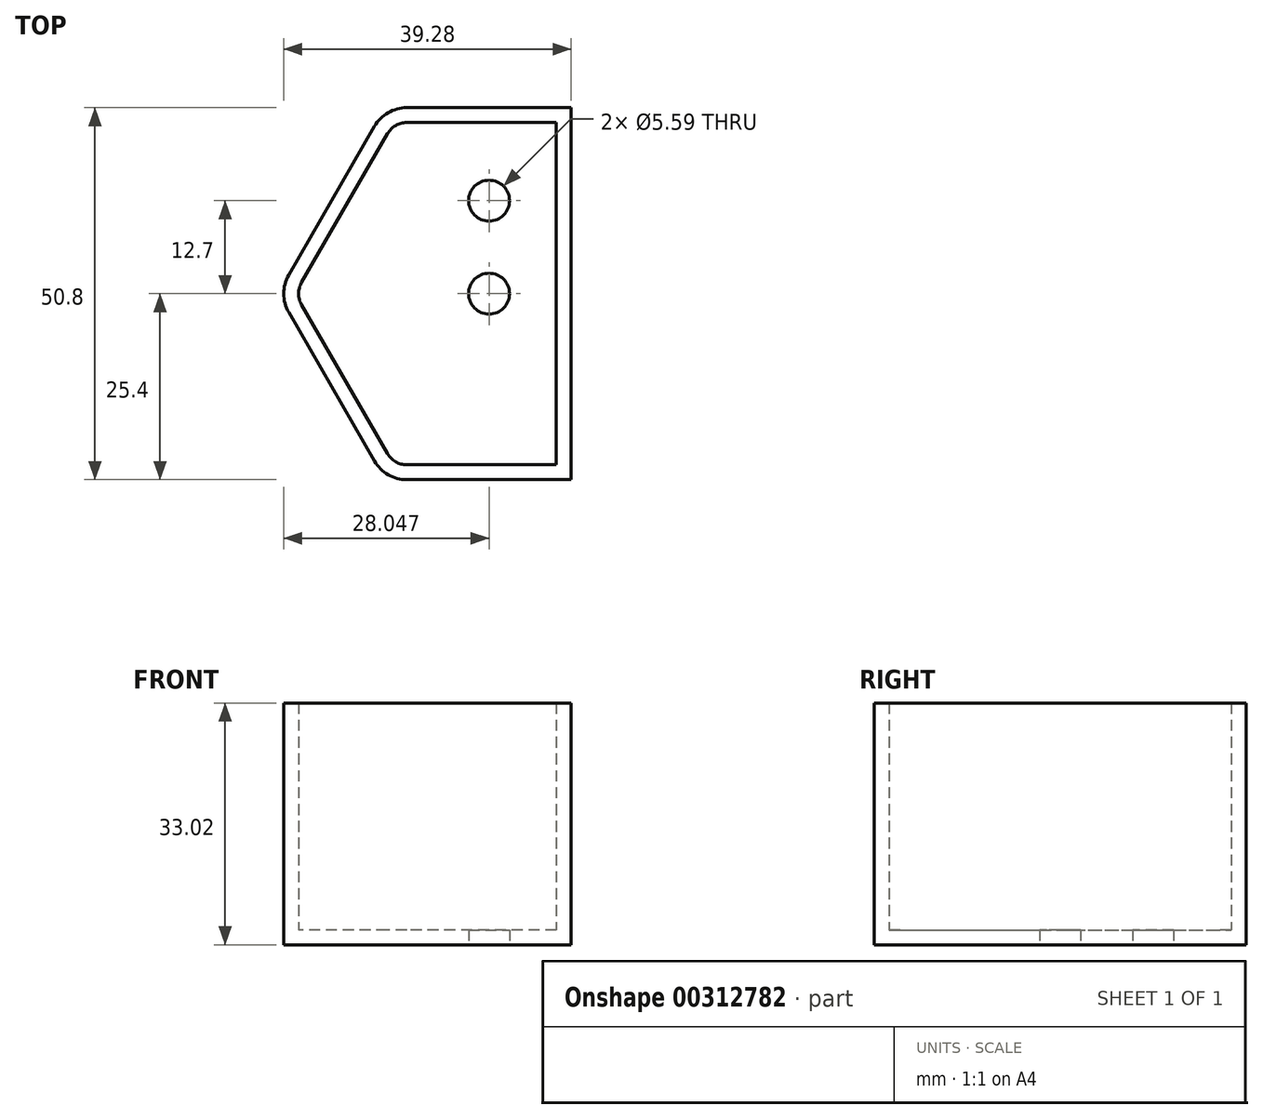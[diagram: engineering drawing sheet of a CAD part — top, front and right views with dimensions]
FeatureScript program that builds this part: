
annotation { "Feature Type Name" : "Feature", "Feature Type Description" : "" }
export const myFeature = defineFeature(function(context is Context, id is Id, definition is map)
    precondition{}
    {
        {
            var Q0;
            Q0=qCreatedBy(makeId("Top.planeOp"),FACE);
            var sketch = newSketch(context, id + "F0", { "sketchPlane" : qUnion([Q0])});
            skLineSegment(sketch, "E0.bottom", {"start": v(0, 0) * mm, "end": v(-25.4, 0) * mm});
            skLineSegment(sketch, "E0.top", {"start": v(0, 50.8) * mm, "end": v(-25.4, 50.8) * mm});
            skLineSegment(sketch, "E0.left", {"start": v(0, 0) * mm, "end": v(0, 50.8) * mm});
            skLineSegment(sketch, "E0.right", {"start": v(-25.4, 0) * mm, "end": v(-25.4, 50.8) * mm});
            skLineSegment(sketch, "E1", {"start": v(-25.4, 0) * mm, "end": v(-40.06, 25.4) * mm});
            skPoint(sketch, "E1.endSnap0", {"position": v(-25.4, 25.4) * mm});
            skLineSegment(sketch, "E2", {"start": v(-40.06, 25.4) * mm, "end": v(-25.4, 50.8) * mm});
            skLineSegment(sketch, "E3", {"start": v(-25.4, 25.4) * mm, "end": v(-40.06, 25.4) * mm});
            skSolve(sketch);
        }
        {
            var Q0;
            {var subQ0=sQuery(id+"F0.wireOp",EDGE,"E1");Q0=makeQuery(id+"F0.imprint","IMPRINT",FACE,{"disambiguationData":[TD([[makeQuery(id+"F0.imprint","IMPRINT",EDGE,{"derivedFrom":subQ0}),-1.0]])]});}
            var Q1;
            {var subQ0=sQuery(id+"F0.wireOp",EDGE,"E2");Q1=makeQuery(id+"F0.imprint","IMPRINT",FACE,{"disambiguationData":[TD([[makeQuery(id+"F0.imprint","IMPRINT",EDGE,{"derivedFrom":subQ0}),-1.0]])]});}
            var Q2;
            {var subQ1=sQuery(id+"F0.wireOp",EDGE,"E0.bottom");Q2=makeQuery(id+"F0.imprint","IMPRINT",FACE,{"disambiguationData":[TD([[makeQuery(id+"F0.imprint","IMPRINT",EDGE,{"derivedFrom":subQ1}),-1.0]])]});}
            extrude(context, id + "F1", {"entities" : qUnion([Q0, Q1, Q2]), "depth" : 33.02 * mm});
        }
        {
            var Q0;
            Q0=makeQuery(id+"F1.opExtrude","SWEPT_EDGE",EDGE,{"disambiguationData":[OSD([sQuery(id+"F0.wireOp",EDGE,"E1"),sQuery(id+"F0.wireOp",EDGE,"E2"),sQuery(id+"F0.wireOp",EDGE,"E3")])]});
            var Q1;
            Q1=makeQuery(id+"F1.opExtrude","SWEPT_EDGE",EDGE,{"disambiguationData":[OSD([sQuery(id+"F0.wireOp",EDGE,"E0.top"),sQuery(id+"F0.wireOp",EDGE,"E0.right"),sQuery(id+"F0.wireOp",EDGE,"E2")])]});
            var Q2;
            Q2=makeQuery(id+"F1.opExtrude","SWEPT_EDGE",EDGE,{"disambiguationData":[OSD([sQuery(id+"F0.wireOp",EDGE,"E0.bottom"),sQuery(id+"F0.wireOp",EDGE,"E0.right"),sQuery(id+"F0.wireOp",EDGE,"E1")])]});
            fillet(context, id + "F2", {"entities" : qUnion([Q0, Q1, Q2]), "radius" : 5.08 * mm, "tangentPropagation" : true, "allowEdgeOverflow" : false});
        }
        {
            var Q0;
            Q0=makeQuery(id+"F1.opExtrude","CAP_FACE",FACE,{"disambiguationData":[OSD([sQuery(id+"F0.wireOp",EDGE,"E0.bottom"),sQuery(id+"F0.wireOp",EDGE,"E0.top"),sQuery(id+"F0.wireOp",EDGE,"E0.left"),sQuery(id+"F0.wireOp",EDGE,"E1"),sQuery(id+"F0.wireOp",EDGE,"E2")])],"isStart":true});
            var sketch = newSketch(context, id + "F3", { "sketchPlane" : qUnion([Q0])});
            skCircle(sketch, "E4", {"center": v(-11.23, -25.4) * mm, "radius": 2.8 * mm});
            skPoint(sketch, "E4.centerSnap0", {"position": v(0, -25.4) * mm});
            skPoint(sketch, "E4.centerSnap1", {"position": v(-11.23, -50.8) * mm});
            skLineSegment(sketch, "E5", {"start": v(0, -50.8) * mm, "end": v(0, -25.4) * mm});
            skCircle(sketch, "E6", {"center": v(-11.23, -38.1) * mm, "radius": 2.8 * mm});
            skPoint(sketch, "E6.centerSnap0", {"position": v(0, -38.1) * mm});
            skSolve(sketch);
        }
        {
            var Q0;
            Q0=makeQuery(id+"F1.opExtrude","CAP_FACE",FACE,{"disambiguationData":[OSD([sQuery(id+"F0.wireOp",EDGE,"E0.bottom"),sQuery(id+"F0.wireOp",EDGE,"E0.top"),sQuery(id+"F0.wireOp",EDGE,"E0.left"),sQuery(id+"F0.wireOp",EDGE,"E1"),sQuery(id+"F0.wireOp",EDGE,"E2")])],"isStart":false});
            shell(context, id + "F4", {"entities" : qUnion([Q0]), "thickness" : 2.03 * mm});
        }
        {
            var Q0;
            Q0=makeQuery(id+"F3.imprint","IMPRINT",FACE,{"disambiguationData":[TD([[makeQuery(id+"F3.imprint","IMPRINT",EDGE,{"derivedFrom":sQuery(id+"F3.wireOp",EDGE,"E4")}),1.0]])]});
            var Q1;
            Q1=makeQuery(id+"F3.imprint","IMPRINT",FACE,{"disambiguationData":[TD([[makeQuery(id+"F3.imprint","IMPRINT",EDGE,{"derivedFrom":sQuery(id+"F3.wireOp",EDGE,"E6")}),1.0]])]});
            extrude(context, id + "F5", {"entities" : qUnion([Q0, Q1]), "operationType" : NewBodyOperationType.REMOVE, "oppositeDirection" : true, "depth" : 2.03 * mm});
        }
    });
